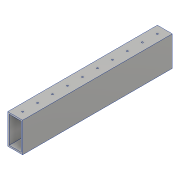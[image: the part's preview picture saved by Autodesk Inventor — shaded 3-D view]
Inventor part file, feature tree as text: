
AUTODESK INVENTOR PART (.ipt)
format: ipt  version: 2018 (Build 220112000, 112)  size: 118,272 bytes
history: native  units: in
note: dims shown in document units (in); Inventor stores cm internally (conversion verified against a paired STEP export)
features: sketch x2, extrude x1, shell x1, hole x1
ambient origin geometry x8: Origin, YZ Plane, XZ Plane, XY Plane, X Axis, Y Axis, Z Axis, Center Point
bodies: Solid1 (feature_tree)
feature tree (5):
  extrude  "Extrusion1"  Depth=2.0in
  shell  "Shell1"  Thickness=10.0in
  hole  "Hole1"  [1 undecoded]
  sketch  "Sketch1"  dims[d0=1.0in d1=2.0in d2=10.0in d3=0.0in]
  sketch  "Sketch2"  dims[d4=0.1in d5=0.5in d6=0.5in d7=14.5669in d9=1.0in d10=0.3937in d12=1.0in d14=0.1in d15=0.75in d16=0.375in d17=0.25in d18=0.5635in d19=2.0in d20=0.8108in]
note: 1 required parameter value undecoded (feature->parameter linkage not recoverable at this tier; creation-order binding heuristic only, values carry confidence <= 0.55)
